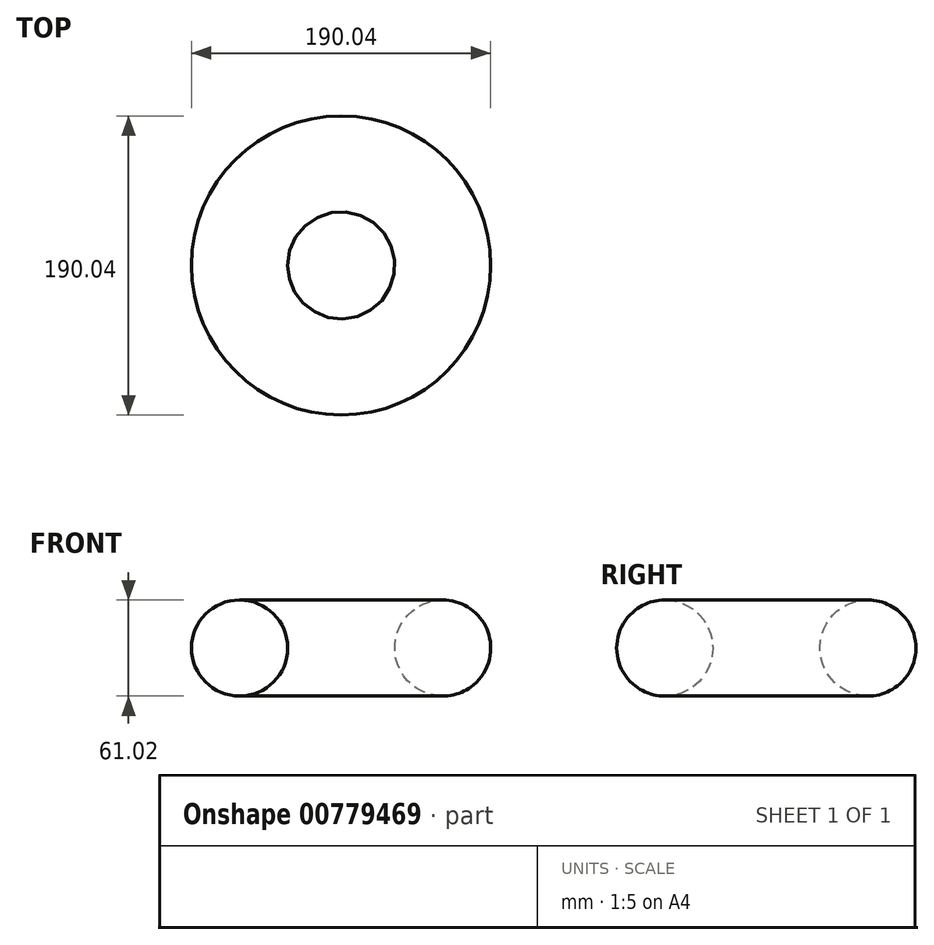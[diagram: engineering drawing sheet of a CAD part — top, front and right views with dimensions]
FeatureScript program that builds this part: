
annotation { "Feature Type Name" : "Feature", "Feature Type Description" : "" }
export const myFeature = defineFeature(function(context is Context, id is Id, definition is map)
    precondition{}
    {
        {
            var Q0;
            Q0=qCreatedBy(makeId("Front.planeOp"),FACE);
            var sketch = newSketch(context, id + "F0", { "sketchPlane" : qUnion([Q0])});
            skCircle(sketch, "E0", {"center": v(0, 0) * mm, "radius": 30.5 * mm});
            skSolve(sketch);
        }
        {
            var Q0;
            Q0=qCreatedBy(makeId("Top.planeOp"),FACE);
            var sketch = newSketch(context, id + "F1", { "sketchPlane" : qUnion([Q0])});
            skCircle(sketch, "E1", {"center": v(64.51, 0) * mm, "radius": 64.51 * mm});
            skSolve(sketch);
        }
        {
            var Q0;
            Q0 = qSketchRegion(id + "F0", true);
            var Q1;
            Q1=sQuery(id+"F1.wireOp",EDGE,"E1");
            revolve(context, id + "F2", {"surfaceOperationType" : NewSurfaceOperationType.NEW, "entities" : qUnion([Q0]), "axis" : qUnion([Q1]), "revolveType" : RevolveType.FULL});
        }
    });
